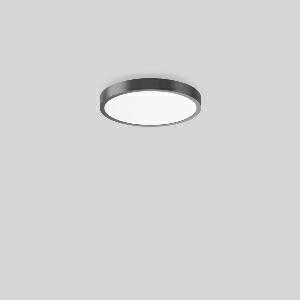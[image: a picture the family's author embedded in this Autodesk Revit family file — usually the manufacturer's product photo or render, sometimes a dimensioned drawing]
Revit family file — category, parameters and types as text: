
# Revit family: triona_round_a_312420_0031_76_fbac
name_source: partatom
category: Lighting Fixtures
units: mm (PartAtom-declared; Revit-internal decimal feet)

## family parameters
Cut with Voids When Loaded = No
Host = Face
Light Source = No
Part Type = Normal
Room Calculation Point = No
Round Connector Dimension = Use Diameter
Shared = No

## types (1)
- TRIONA round A (1 x LED Modul 830, 5850 lm, 3000)
    Apparent Load = 64 VA
    CIE Flux Codes = 49 80 96 82 100
    Color Rendering = 80
    Color Temperature = 3000
    Default Elevation = 1800 mm
    Description = Series: TRIONA round
Decorative round LED surface-mounted luminaire. Flat, seamless frame: aluminium extrusion profile, powder coated. Cover made of sheet steel, powder-coated. Direct light emission through a diffuser plastic opal. Indirect light emission through a flush diffuser made of satin-finish plastic. Lightguide and diffuser made of non-yellowing plastic (PMMA). Lateral light emission (RZB SIDELITE technology) for above-average homogeneous light distribution. Direct 70%, indirect 30% light emission. Suitable for Ceiling mounting, Wall (surface). Tool-free mounting via bayonet connection. Electronic ballast included. Very easy installation thanks to Plug+Play connection. 
Colour: anthracite metallic (DB703)
Diameter: 461 mm
Height: 88 mm
Lamp: LED
Socket: without socket
Colour temperature: 3000K
Colour rendering index (CRI): 80
System power: 64 W
Rated luminous flux: 5850 lm
Luminous efficiency: 91 lm/W
Control gear: Converter, dimmable, DALI
Protection class: I
Type of protection: IP 20
    Height = 88 mm
    Lamp = 1 x LED Modul 830
    Lamp Light Flux = 5850 lm
    Lamp count = 1
    Length = 461 mm
    Lifetime = 50000 h
    Luminous efficacy = 91 lm/W
    Manufacturer = RZB
    ModVariant = No
    Model = 312420.0031.76
    Mounting Place = Ceiling
    Mounting Type = Surface mounted
    Number of Poles = 1
    OnlyDefault = Yes
    Power Factor = 1
    Product Name = TRIONA round A
    Product group = Surface mounted modular luminaires
    ProductGroupID = 306
    Protection Class = Protection class I
    Protection Degree = IP 20
    RLX_Detail_Level = 1
    RLX_Emergency_Light_Flux = 0 lm
    RLX_Emergency_Type = 0
    RLX_Emergency_Type_DB = No
    RlxData = <blob elided: 39385 chars, md5=38af05c2>
    Socket = socket
    Standby Power = 0 W
    System Light Flux = 5850 lm
    System Power = 64 W
    Type Comments = Product without accessories
    Type Image = 312420.0031.jpg
    URL = http://relux.com
    VarID = ---
    Voltage = 230 V
    Voltage Range = 220-240 V
    Weight = 0.00 kg
    Width = 0 mm  [stored 0 ft]

note: [stored X ft] marks values corroborated as IEEE doubles in the binary element streams (Revit-internal decimal feet)

## geometry (parser evidence)
native form markers: Blend x4, Sweep x13
no freeform markers — native parametric forms only
